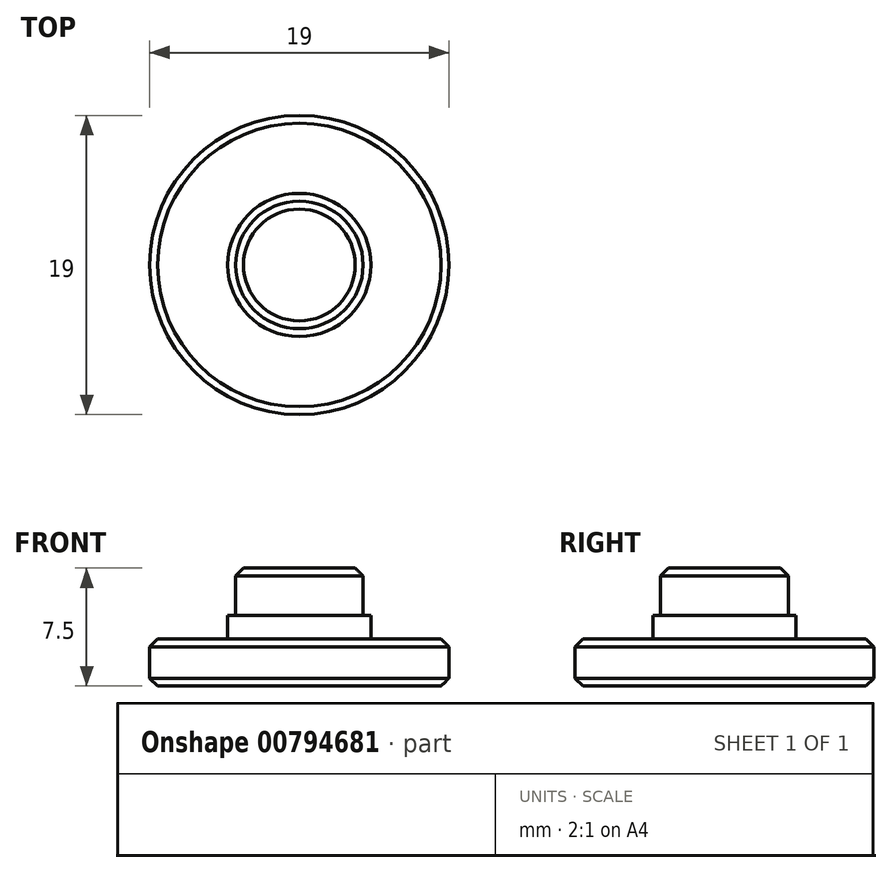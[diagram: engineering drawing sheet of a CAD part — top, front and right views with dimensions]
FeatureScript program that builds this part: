
annotation { "Feature Type Name" : "Feature", "Feature Type Description" : "" }
export const myFeature = defineFeature(function(context is Context, id is Id, definition is map)
    precondition{}
    {
        {
            var Q0;
            Q0=qCreatedBy(makeId("Top.planeOp"),FACE);
            var sketch = newSketch(context, id + "F0", { "sketchPlane" : qUnion([Q0])});
            skCircle(sketch, "E0", {"center": v(0, 0) * mm, "radius": 9.5 * mm});
            skSolve(sketch);
        }
        {
            var Q0;
            Q0=qSketchRegion(id+"F0",true);
            extrude(context, id + "F1", {"entities" : qUnion([Q0]), "depth" : 3 * mm, "offsetDistance" : 25 * mm});
        }
        {
            var Q0;
            Q0=makeQuery(id+"F1.opExtrude","CAP_FACE",FACE,{"disambiguationData":[OSD([sQuery(id+"F0.wireOp",EDGE,"E0")])],"isStart":false});
            var sketch = newSketch(context, id + "F2", { "sketchPlane" : qUnion([Q0])});
            skCircle(sketch, "E1", {"center": v(0, 0) * mm, "radius": 4.05 * mm});
            skSolve(sketch);
        }
        {
            var Q0;
            Q0=qSketchRegion(id+"F2",true);
            extrude(context, id + "F3", {"entities" : qUnion([Q0]), "operationType" : NewBodyOperationType.ADD, "depth" : 4.5 * mm, "offsetDistance" : 25 * mm});
        }
        {
            var Q0;
            Q0=makeQuery(id+"F3.opExtrude","CAP_EDGE",EDGE,{"disambiguationData":[OSD([sQuery(id+"F2.wireOp",EDGE,"E1")])],"isStart":false});
            var Q1;
            Q1=makeQuery(id+"F1.opExtrude","CAP_EDGE",EDGE,{"disambiguationData":[OSD([sQuery(id+"F0.wireOp",EDGE,"E0")])],"isStart":false});
            var Q2;
            Q2=makeQuery(id+"F1.opExtrude","CAP_EDGE",EDGE,{"disambiguationData":[OSD([sQuery(id+"F0.wireOp",EDGE,"E0")])],"isStart":true});
            chamfer(context, id + "F4", {"entities" : qUnion([Q0, Q1, Q2]), "width" : 0.5 * mm, "tangentPropagation" : true});
        }
        {
            var Q0;
            Q0=makeQuery(id+"F1.opExtrude","CAP_FACE",FACE,{"disambiguationData":[OSD([sQuery(id+"F0.wireOp",EDGE,"E0")])],"isStart":false});
            var sketch = newSketch(context, id + "F5", { "sketchPlane" : qUnion([Q0])});
            skCircle(sketch, "E2", {"center": v(0, 0) * mm, "radius": 4.55 * mm});
            skSolve(sketch);
        }
        {
            var Q0;
            Q0=qSketchRegion(id+"F5",true);
            extrude(context, id + "F6", {"entities" : qUnion([Q0]), "operationType" : NewBodyOperationType.ADD, "depth" : 1.5 * mm, "offsetDistance" : 25 * mm});
        }
    });
